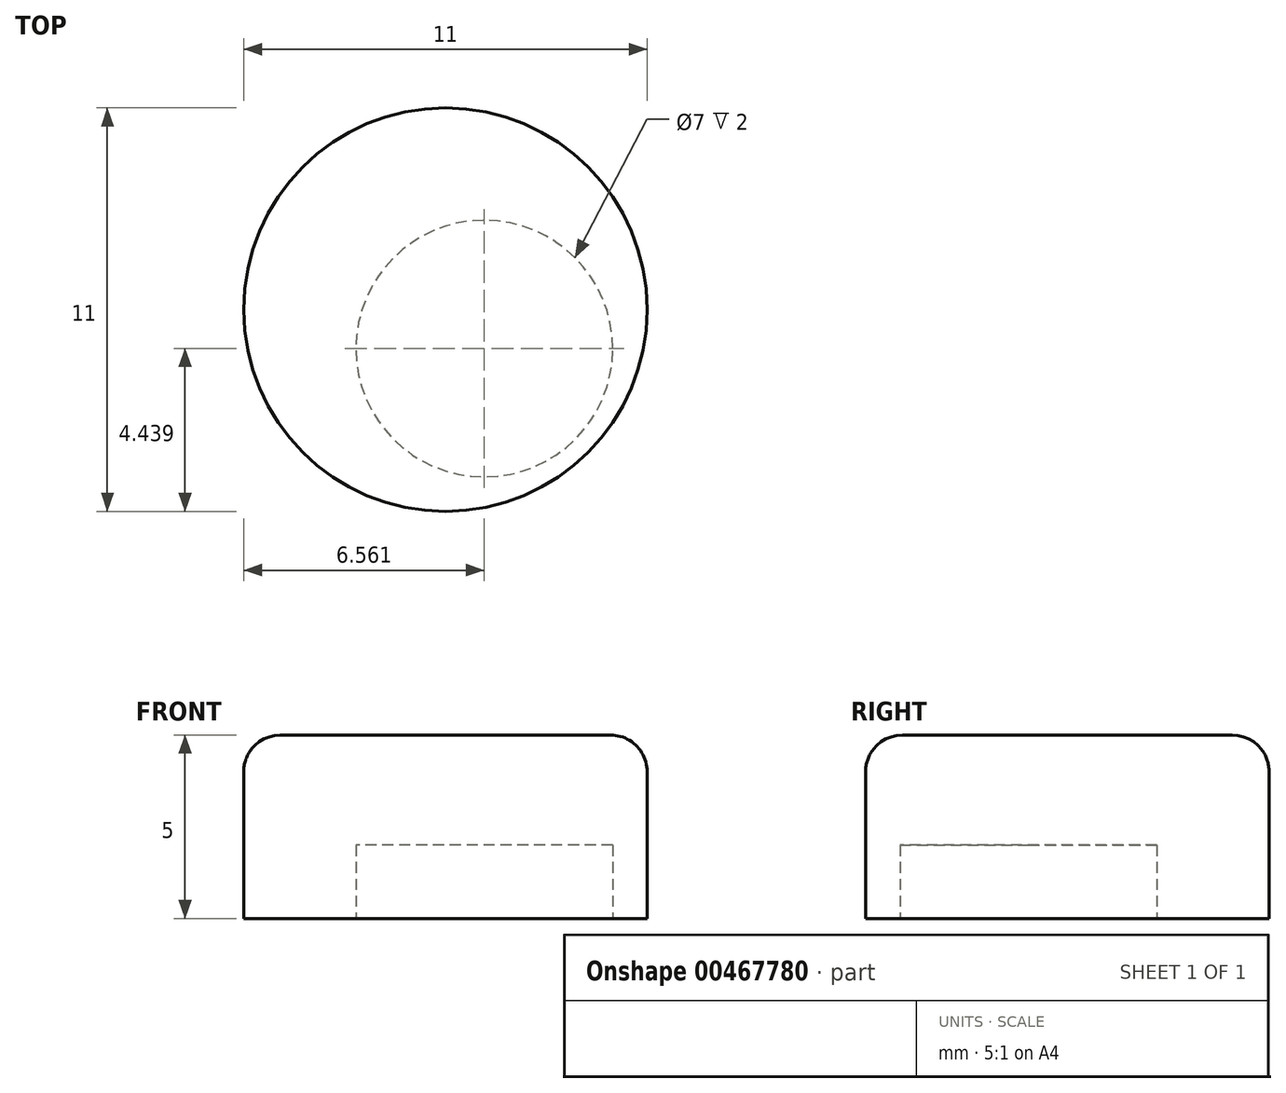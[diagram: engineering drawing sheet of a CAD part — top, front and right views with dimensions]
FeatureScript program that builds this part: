
annotation { "Feature Type Name" : "Feature", "Feature Type Description" : "" }
export const myFeature = defineFeature(function(context is Context, id is Id, definition is map)
    precondition{}
    {
        {
            var Q0;
            Q0=qCreatedBy(makeId("Top.planeOp"),FACE);
            var sketch = newSketch(context, id + "F0", { "sketchPlane" : qUnion([Q0])});
            skCircle(sketch, "E0", {"center": v(0, 0) * mm, "radius": 5.5 * mm});
            skLineSegment(sketch, "E1", {"start": v(0, 0) * mm, "end": v(3.89, -3.89) * mm, "construction": true});
            skLineSegment(sketch, "E2", {"start": v(-5.5, 0) * mm, "end": v(5.5, 0) * mm, "construction": true});
            skCircle(sketch, "E3", {"center": v(1.06, -1.06) * mm, "radius": 3.5 * mm});
            skSolve(sketch);
        }
        {
            var Q0;
            Q0=makeQuery(id+"F0.imprint","IMPRINT",FACE,{"disambiguationData":[TD([[makeQuery(id+"F0.imprint","IMPRINT",EDGE,{"derivedFrom":sQuery(id+"F0.wireOp",EDGE,"E3")}),1.0]])]});
            var Q1;
            Q1=makeQuery(id+"F0.imprint","IMPRINT",FACE,{"disambiguationData":[TD([[makeQuery(id+"F0.imprint","IMPRINT",EDGE,{"derivedFrom":sQuery(id+"F0.wireOp",EDGE,"E0")}),1.0]])]});
            var Q2;
            Q2=sQuery(id+"F0.wireOp",EDGE,"E0");
            extrude(context, id + "F1", {"entities" : qUnion([Q0, Q1]), "surfaceEntities" : qUnion([Q2]), "depth" : 3 * mm});
        }
        {
            var Q0;
            Q0=makeQuery(id+"F0.imprint","IMPRINT",FACE,{"disambiguationData":[TD([[makeQuery(id+"F0.imprint","IMPRINT",EDGE,{"derivedFrom":sQuery(id+"F0.wireOp",EDGE,"E3")}),1.0]])]});
            extrude(context, id + "F2", {"entities" : qUnion([Q0]), "operationType" : NewBodyOperationType.REMOVE, "offsetDistance" : 25 * mm, "depth" : 2 * mm});
        }
        {
            var Q0;
            Q0=qCreatedBy(makeId("Front.planeOp"),FACE);
            var sketch = newSketch(context, id + "F3", { "sketchPlane" : qUnion([Q0])});
            skLineSegment(sketch, "E4.0", {"start": v(-5.5, 3) * mm, "end": v(0, 3) * mm});
            skLineSegment(sketch, "E5", {"start": v(0, 3) * mm, "end": v(0, 5) * mm});
            skLineSegment(sketch, "E6", {"start": v(0, 5) * mm, "end": v(2.15, 5) * mm, "construction": true});
            skLineSegment(sketch, "E7", {"start": v(-5.5, 3) * mm, "end": v(-5.5, 5) * mm});
            skLineSegment(sketch, "E8", {"start": v(-5.5, 5) * mm, "end": v(0, 5) * mm});
            skSolve(sketch);
        }
        {
            var Q0;
            Q0=makeQuery(id+"F3.imprint","IMPRINT",FACE,{"disambiguationData":[TD([[makeQuery(id+"F3.imprint","IMPRINT",EDGE,{"derivedFrom":sQuery(id+"F3.wireOp",EDGE,"E4.0")}),1.0]])]});
            var Q1;
            Q1=sQuery(id+"F3.wireOp",EDGE,"E5");
            revolve(context, id + "F4", {"operationType" : NewBodyOperationType.ADD, "entities" : qUnion([Q0]), "axis" : qUnion([Q1]), "revolveType" : RevolveType.FULL});
        }
        {
            var Q0;
            Q0=makeQuery(id+"F4.opRevolve","SWEPT_EDGE",EDGE,{"disambiguationData":[OSD([sQuery(id+"F3.wireOp",EDGE,"E7"),sQuery(id+"F3.wireOp",EDGE,"E8")])]});
            fillet(context, id + "F5", {"entities" : qUnion([Q0]), "radius" : 1 * mm, "tangentPropagation" : true, "allowEdgeOverflow" : false});
        }
    });
